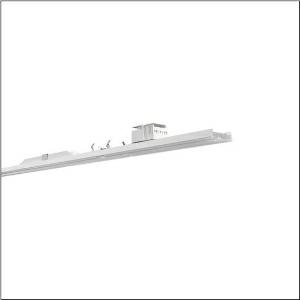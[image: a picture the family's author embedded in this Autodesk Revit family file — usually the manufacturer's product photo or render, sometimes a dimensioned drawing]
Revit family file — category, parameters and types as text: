
# Revit family: licross_r__11_recessed_mo_51tl14cn475fd_06e4
name_source: partatom
category: Lighting Fixtures
units: mm (PartAtom-declared; Revit-internal decimal feet)

## family parameters
Cut with Voids When Loaded = No
Host = Face
Light Source = No
Part Type = Normal
Room Calculation Point = No
Round Connector Dimension = Use Diameter
Shared = No

## types (1)
- --- (1 x LED, 3150 lm, 22.1 W, 4000K)
    Apparent Load = 22 VA
    CIE Flux Codes = 56 84 97 100 100
    Color Rendering = 80
    Color Temperature = 4000K
    Default Elevation = 1800 mm
    Description = Licross® 11 Recessed MOluminaire insert, length: 1.500mm, width: 66mm, height: 67mm, LED rated luminous flux: 7.640lm, light colour: 840, control gear: ON/OFF Multilumen, CLOi, control gear: ECG Multilumen, with plug, 6-pole, with phase selection, mains connection: 220..240V, AC/DC, 0/50..60Hz, without changeover relay, for emergency light function, for central battery installations according to DIN EN 60598-2-22, halogen-free wiring, primary optical cover: cover, of PMMA, light emission: direct distribution, primary light characteristic: asymmetric, protection rating (complete): IP40, insulation class (complete): insulation class I (protective earthing), certification: CE, ENEC, VDE, protection symbol: D if used in an environment without relevant dust loads with corresponding accessories, permissible ambient temperature for indoor applications: -35..+40°C, standard: EN 60598-2-22, reducing of maximum allowable ambient temperature of 5°C with ceiling mounting, corresponds to IFS (International Featured Standards) requirements for safety and quality in the food industry, packaging unit: 1 piece
    Height = 58 mm
    Lamp = 1 x LED
    Lamp Light Flux = 3150 lm
    Lamp Power = 22.1 W
    Lamp count = 1
    Length = 1500 mm
    Luminous efficacy = 143 lm/W
    Manufacturer = Siteco
    ModVariant = No
    Model = 51TL14CN475FD
    Mounting Place = Ceiling
    Mounting Type = Pendant
    Number of Poles = 1
    OnlyDefault = Yes
    Power Factor = 1
    Product Name = Licross® 11 Recessed MO
    Product group = luminaire insert
    ProductGroupID = 902
    Protection Class = Protection class I
    Protection Degree = IP 40
    RLX_Detail_Level = 1
    RlxData = <blob elided: 21013 chars, md5=e1259946>
    Socket = socket
    Standby Power = 0 W
    System Light Flux = 3150 lm
    System Power = 22 W
    Type Comments = : DC mode (central or group accumulator) initial emergency light level
    Type Image = l_1266722.jpg
    URL = http://relux.com
    VarID = @adj_134347
    Voltage = 0 V
    Weight = 0.00 kg
    Width = 66 mm

## geometry (parser evidence)
native form markers: Blend x4, Sweep x11
no freeform markers — native parametric forms only
